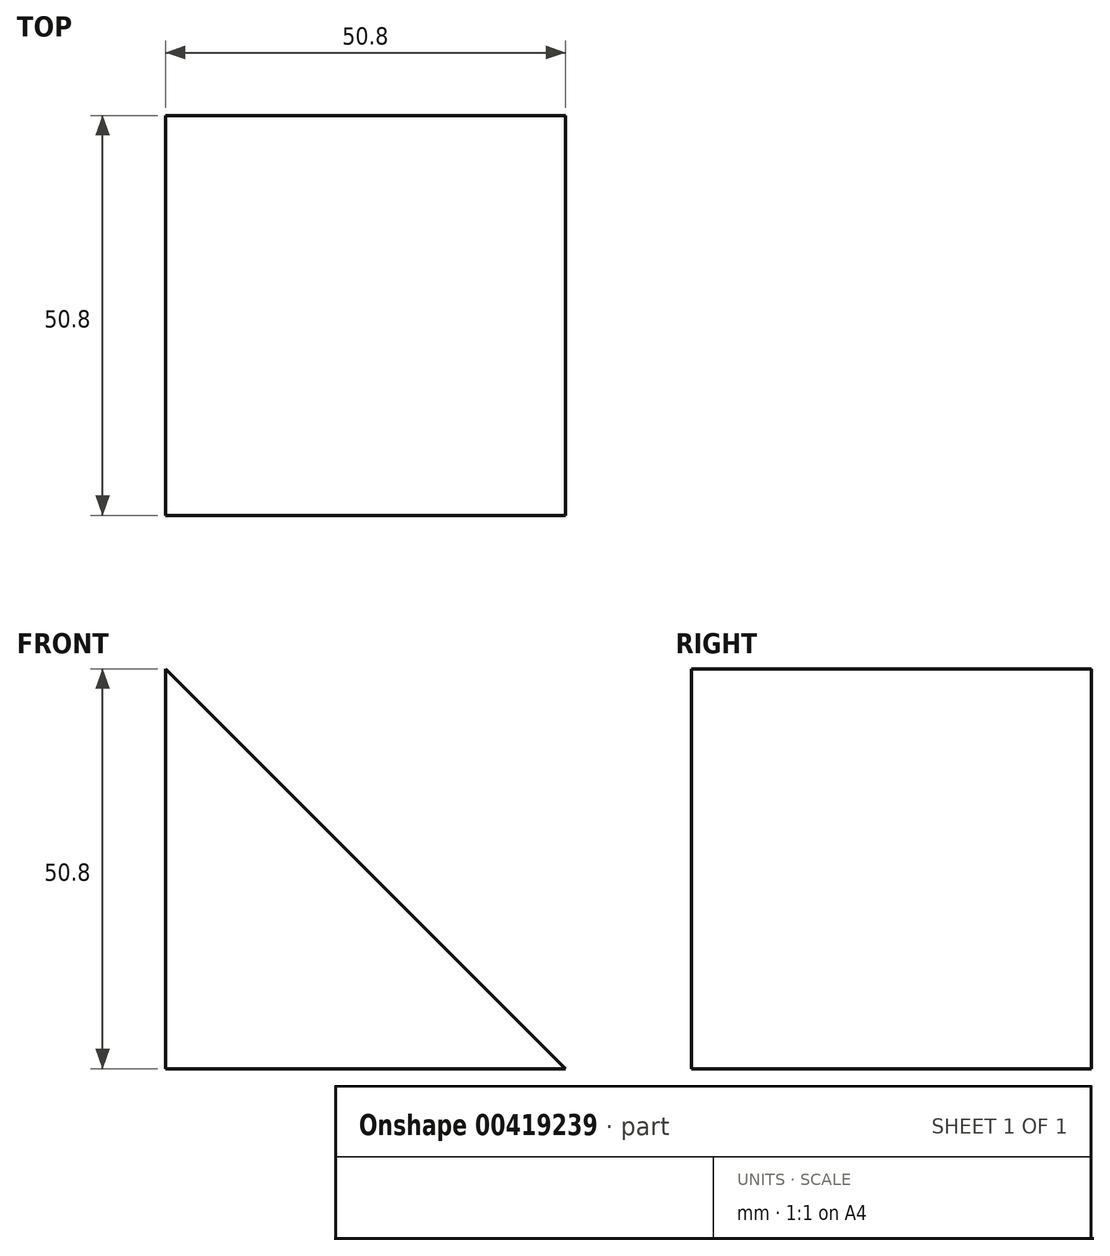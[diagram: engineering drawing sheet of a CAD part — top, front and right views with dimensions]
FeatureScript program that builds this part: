
annotation { "Feature Type Name" : "Feature", "Feature Type Description" : "" }
export const myFeature = defineFeature(function(context is Context, id is Id, definition is map)
    precondition{}
    {
        {
            var Q0;
            Q0=qCreatedBy(makeId("Front.planeOp"),FACE);
            var sketch = newSketch(context, id + "F0", { "sketchPlane" : qUnion([Q0])});
            skLineSegment(sketch, "E0", {"start": v(0, 0) * mm, "end": v(0, 50.8) * mm});
            skLineSegment(sketch, "E1", {"start": v(0, 50.8) * mm, "end": v(50.8, 0) * mm});
            skLineSegment(sketch, "E2", {"start": v(50.8, 0) * mm, "end": v(0, 0) * mm});
            skSolve(sketch);
        }
        {
            var Q0;
            Q0 = qSketchRegion(id + "F0", true);
            extrude(context, id + "F1", {"entities" : qUnion([Q0]), "depth" : 50.8 * mm});
        }
    });
